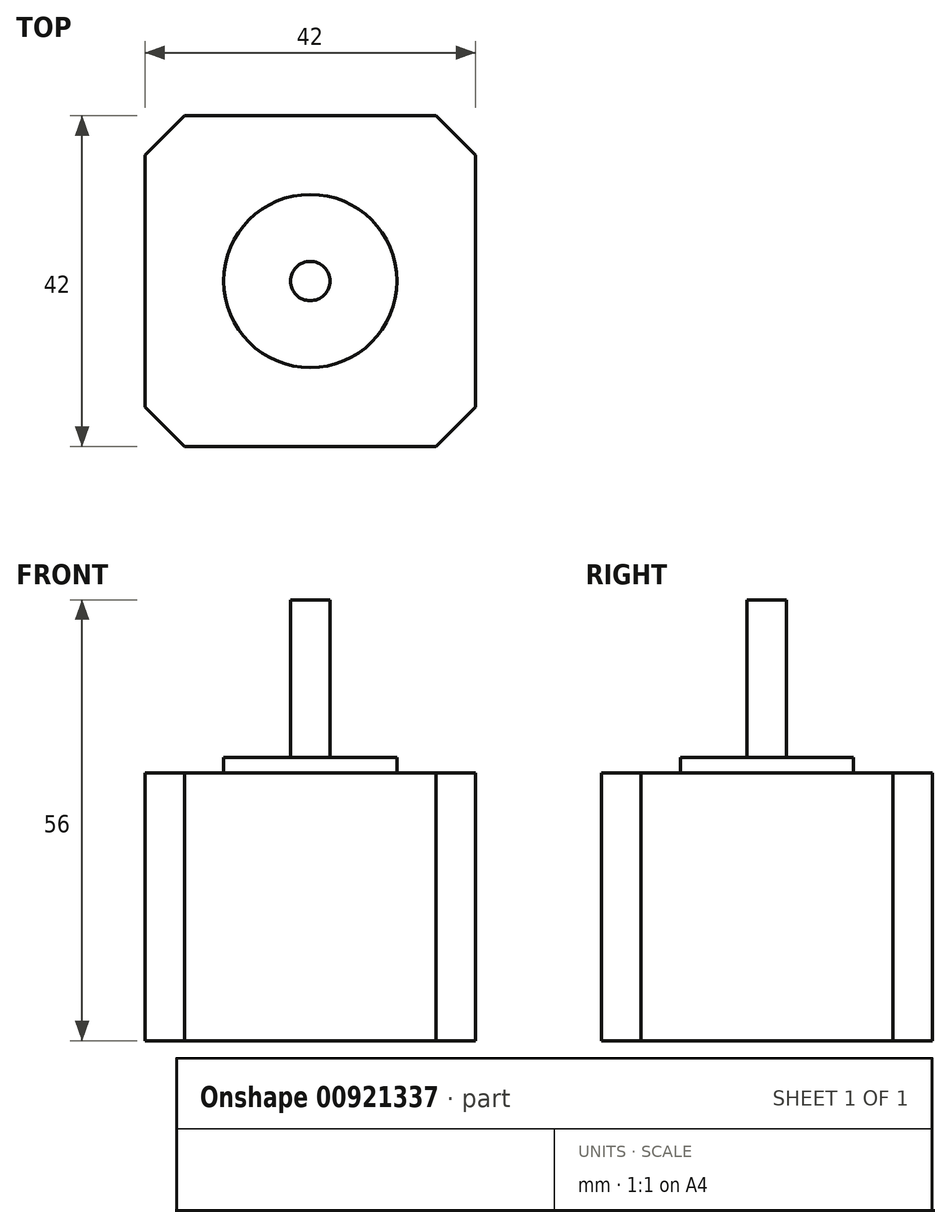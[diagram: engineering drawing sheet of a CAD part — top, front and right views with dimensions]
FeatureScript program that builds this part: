
annotation { "Feature Type Name" : "Feature", "Feature Type Description" : "" }
export const myFeature = defineFeature(function(context is Context, id is Id, definition is map)
    precondition{}
    {
        {
            var Q0;
            Q0=qCreatedBy(makeId("Top.planeOp"),FACE);
            var sketch = newSketch(context, id + "F0", { "sketchPlane" : qUnion([Q0])});
            skLineSegment(sketch, "E0.bottom", {"start": v(21, -21) * mm, "end": v(-21, -21) * mm});
            skLineSegment(sketch, "E0.top", {"start": v(21, 21) * mm, "end": v(-21, 21) * mm});
            skLineSegment(sketch, "E0.left", {"start": v(21, -21) * mm, "end": v(21, 21) * mm});
            skLineSegment(sketch, "E0.right", {"start": v(-21, -21) * mm, "end": v(-21, 21) * mm});
            skPoint(sketch, "E0.middle", {"position": v(0, 0) * mm});
            skSolve(sketch);
        }
        {
            var Q0;
            Q0=makeQuery(id+"F0.imprint","IMPRINT",FACE,{"disambiguationData":[TD([[makeQuery(id+"F0.imprint","IMPRINT",EDGE,{"derivedFrom":sQuery(id+"F0.wireOp",EDGE,"E0.bottom")}),-1.0]])]});
            extrude(context, id + "F1", {"entities" : qUnion([Q0]), "depth" : 34 * mm, "offsetDistance" : 25 * mm});
        }
        {
            var Q0;
            Q0=makeQuery(id+"F1.opExtrude","CAP_FACE",FACE,{"disambiguationData":[OSD([sQuery(id+"F0.wireOp",EDGE,"E0.bottom"),sQuery(id+"F0.wireOp",EDGE,"E0.top"),sQuery(id+"F0.wireOp",EDGE,"E0.left"),sQuery(id+"F0.wireOp",EDGE,"E0.right")])],"isStart":false});
            var sketch = newSketch(context, id + "F2", { "sketchPlane" : qUnion([Q0])});
            skCircle(sketch, "E1", {"center": v(0, 0) * mm, "radius": 11 * mm});
            skSolve(sketch);
        }
        {
            var Q0;
            Q0=makeQuery(id+"F2.imprint","IMPRINT",FACE,{"disambiguationData":[TD([[makeQuery(id+"F2.imprint","IMPRINT",EDGE,{"derivedFrom":sQuery(id+"F2.wireOp",EDGE,"E1")}),1.0]])]});
            extrude(context, id + "F3", {"entities" : qUnion([Q0]), "operationType" : NewBodyOperationType.ADD, "depth" : 2 * mm, "offsetDistance" : 25 * mm});
        }
        {
            var Q0;
            Q0=makeQuery(id+"F3.opExtrude","CAP_FACE",FACE,{"disambiguationData":[OSD([sQuery(id+"F2.wireOp",EDGE,"E1")])],"isStart":false});
            var sketch = newSketch(context, id + "F4", { "sketchPlane" : qUnion([Q0])});
            skCircle(sketch, "E2", {"center": v(0, 0) * mm, "radius": 2.5 * mm});
            skSolve(sketch);
        }
        {
            var Q0;
            Q0=makeQuery(id+"F4.imprint","IMPRINT",FACE,{"disambiguationData":[TD([[makeQuery(id+"F4.imprint","IMPRINT",EDGE,{"derivedFrom":sQuery(id+"F4.wireOp",EDGE,"E2")}),1.0]])]});
            extrude(context, id + "F5", {"entities" : qUnion([Q0]), "operationType" : NewBodyOperationType.ADD, "depth" : 20 * mm, "offsetDistance" : 25 * mm});
        }
        {
            var Q0;
            Q0=makeQuery(id+"F1.opExtrude","SWEPT_EDGE",EDGE,{"disambiguationData":[OSD([sQuery(id+"F0.wireOp",EDGE,"E0.top"),sQuery(id+"F0.wireOp",EDGE,"E0.right")])]});
            var Q1;
            Q1=makeQuery(id+"F1.opExtrude","SWEPT_EDGE",EDGE,{"disambiguationData":[OSD([sQuery(id+"F0.wireOp",EDGE,"E0.top"),sQuery(id+"F0.wireOp",EDGE,"E0.left")])]});
            var Q2;
            Q2=makeQuery(id+"F1.opExtrude","SWEPT_EDGE",EDGE,{"disambiguationData":[OSD([sQuery(id+"F0.wireOp",EDGE,"E0.bottom"),sQuery(id+"F0.wireOp",EDGE,"E0.left")])]});
            var Q3;
            Q3=makeQuery(id+"F1.opExtrude","SWEPT_EDGE",EDGE,{"disambiguationData":[OSD([sQuery(id+"F0.wireOp",EDGE,"E0.bottom"),sQuery(id+"F0.wireOp",EDGE,"E0.right")])]});
            chamfer(context, id + "F6", {"entities" : qUnion([Q0, Q1, Q2, Q3]), "width" : 5 * mm, "tangentPropagation" : true});
        }
    });
